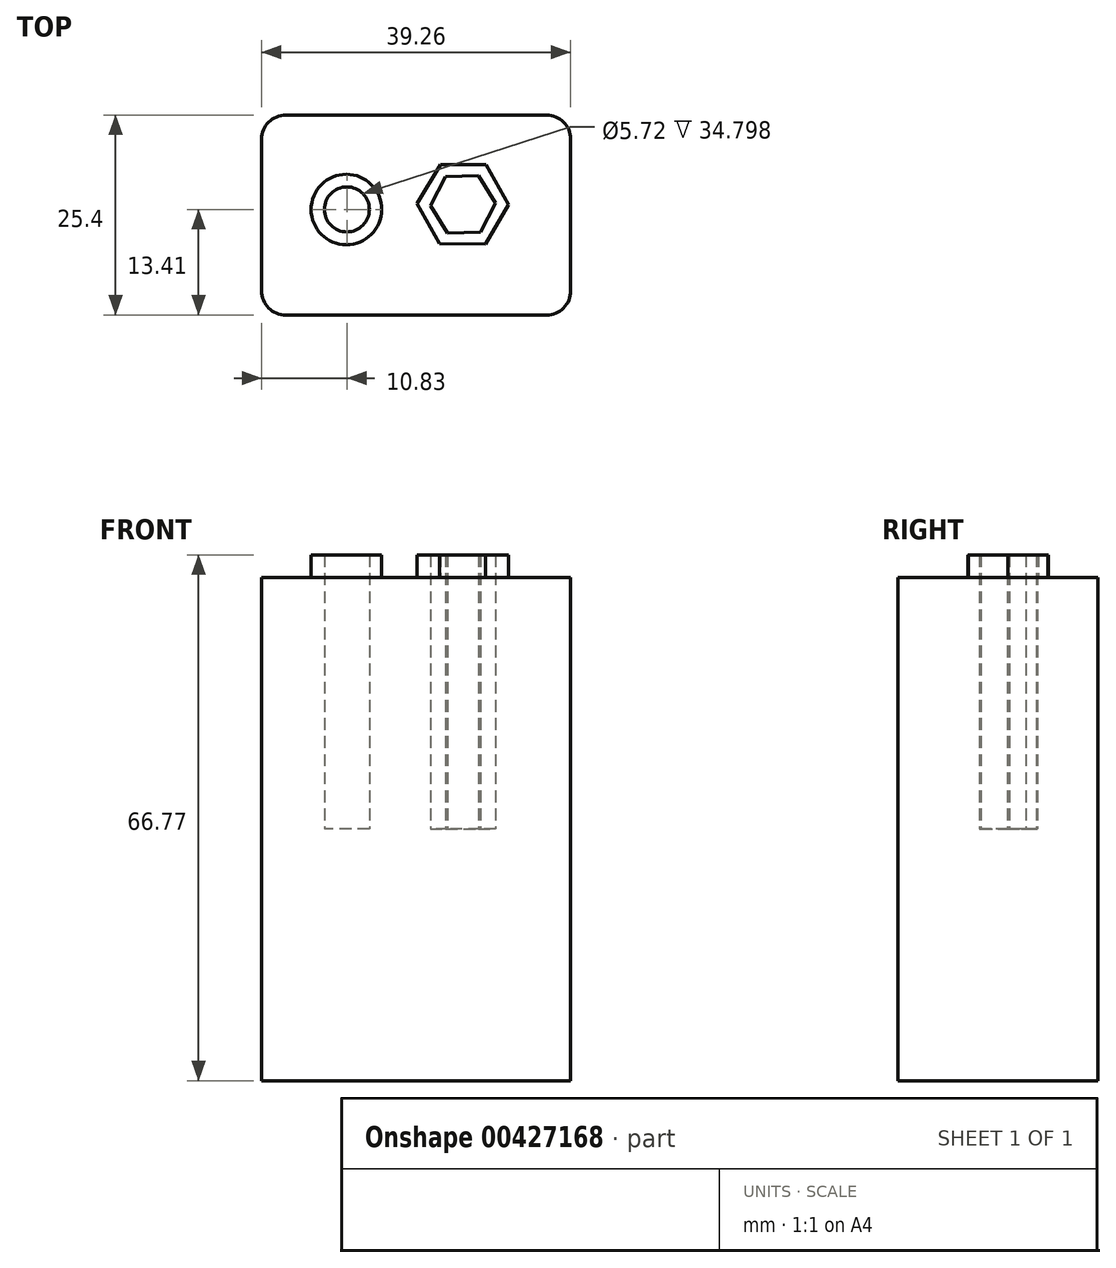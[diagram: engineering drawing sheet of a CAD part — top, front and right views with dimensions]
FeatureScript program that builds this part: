
annotation { "Feature Type Name" : "Feature", "Feature Type Description" : "" }
export const myFeature = defineFeature(function(context is Context, id is Id, definition is map)
    precondition{}
    {
        {
            var Q0;
            Q0=qCreatedBy(makeId("Front.planeOp"),FACE);
            var sketch = newSketch(context, id + "F0", { "sketchPlane" : qUnion([Q0])});
            skLineSegment(sketch, "E0.bottom", {"start": v(-19.63, 31.97) * mm, "end": v(19.63, 31.97) * mm});
            skLineSegment(sketch, "E0.top", {"start": v(-19.63, -31.97) * mm, "end": v(19.63, -31.97) * mm});
            skLineSegment(sketch, "E0.left", {"start": v(-19.63, 31.97) * mm, "end": v(-19.63, -31.97) * mm});
            skLineSegment(sketch, "E0.right", {"start": v(19.63, 31.97) * mm, "end": v(19.63, -31.97) * mm});
            skPoint(sketch, "E0.middle", {"position": v(0, 0) * mm});
            skSolve(sketch);
        }
        {
            var Q0;
            Q0 = qSketchRegion(id + "F0", true);
            extrude(context, id + "F1", {"entities" : qUnion([Q0]), "depth" : 25.4 * mm});
        }
        {
            var Q0;
            Q0=makeQuery(id+"F1.opExtrude","CAP_EDGE",EDGE,{"disambiguationData":[OSD([sQuery(id+"F0.wireOp",EDGE,"E0.left")])],"isStart":false});
            var Q1;
            Q1=makeQuery(id+"F1.opExtrude","CAP_EDGE",EDGE,{"disambiguationData":[OSD([sQuery(id+"F0.wireOp",EDGE,"E0.right")])],"isStart":true});
            var Q2;
            Q2=makeQuery(id+"F1.opExtrude","CAP_EDGE",EDGE,{"disambiguationData":[OSD([sQuery(id+"F0.wireOp",EDGE,"E0.right")])],"isStart":false});
            var Q3;
            Q3=makeQuery(id+"F1.opExtrude","CAP_EDGE",EDGE,{"disambiguationData":[OSD([sQuery(id+"F0.wireOp",EDGE,"E0.left")])],"isStart":true});
            fillet(context, id + "F2", {"entities" : qUnion([Q0, Q1, Q2, Q3]), "radius" : 3.07 * mm, "tangentPropagation" : true, "allowEdgeOverflow" : false});
        }
        {
            var Q0;
            Q0=qCreatedBy(makeId("Top.planeOp"),FACE);
            var sketch = newSketch(context, id + "F3", { "sketchPlane" : qUnion([Q0])});
            skCircle(sketch, "E1", {"center": v(-8.87, -12) * mm, "radius": 4.47 * mm});
            skSolve(sketch);
        }
        {
            var Q0;
            Q0 = qSketchRegion(id + "F3", true);
            extrude(context, id + "F4", {"entities" : qUnion([Q0]), "operationType" : NewBodyOperationType.ADD, "depth" : 34.8 * mm});
        }
        {
            var Q0;
            Q0=qCreatedBy(makeId("Top.planeOp"),FACE);
            var sketch = newSketch(context, id + "F5", { "sketchPlane" : qUnion([Q0])});
            skCircle(sketch, "E2.cCircle", {"center": v(5.94, -11.33) * mm, "radius": 5.81 * mm, "construction": true});
            skLineSegment(sketch, "E2.0", {"start": v(8.8, -16.39) * mm, "end": v(2.99, -16.34) * mm});
            skLineSegment(sketch, "E2.1", {"start": v(2.99, -16.34) * mm, "end": v(0.13, -11.28) * mm});
            skLineSegment(sketch, "E2.2", {"start": v(0.13, -11.28) * mm, "end": v(3.08, -6.27) * mm});
            skLineSegment(sketch, "E2.3", {"start": v(3.08, -6.27) * mm, "end": v(8.9, -6.32) * mm});
            skLineSegment(sketch, "E2.4", {"start": v(8.9, -6.32) * mm, "end": v(11.75, -11.38) * mm});
            skLineSegment(sketch, "E2.5", {"start": v(11.75, -11.38) * mm, "end": v(8.8, -16.39) * mm});
            skSolve(sketch);
        }
        {
            var Q0;
            Q0 = qSketchRegion(id + "F5", true);
            extrude(context, id + "F6", {"entities" : qUnion([Q0]), "operationType" : NewBodyOperationType.ADD, "depth" : 34.8 * mm});
        }
        {
            var Q0;
            Q0=qCreatedBy(makeId("Top.planeOp"),FACE);
            var sketch = newSketch(context, id + "F7", { "sketchPlane" : qUnion([Q0])});
            skCircle(sketch, "E3", {"center": v(-8.8, -11.99) * mm, "radius": 2.86 * mm});
            skCircle(sketch, "E4.cCircle", {"center": v(5.94, -11.33) * mm, "radius": 4.15 * mm, "construction": true});
            skLineSegment(sketch, "E4.0", {"start": v(3.74, -7.8) * mm, "end": v(7.89, -7.66) * mm});
            skLineSegment(sketch, "E4.1", {"start": v(7.89, -7.66) * mm, "end": v(10.09, -11.18) * mm});
            skLineSegment(sketch, "E4.2", {"start": v(10.09, -11.18) * mm, "end": v(8.14, -14.85) * mm});
            skLineSegment(sketch, "E4.3", {"start": v(8.14, -14.85) * mm, "end": v(4, -15) * mm});
            skLineSegment(sketch, "E4.4", {"start": v(4, -15) * mm, "end": v(1.8, -11.48) * mm});
            skLineSegment(sketch, "E4.5", {"start": v(1.8, -11.48) * mm, "end": v(3.74, -7.8) * mm});
            skSolve(sketch);
        }
        {
            var Q0;
            Q0 = qSketchRegion(id + "F7", true);
            extrude(context, id + "F8", {"entities" : qUnion([Q0]), "operationType" : NewBodyOperationType.REMOVE, "depth" : 35.3 * mm});
        }
    });
